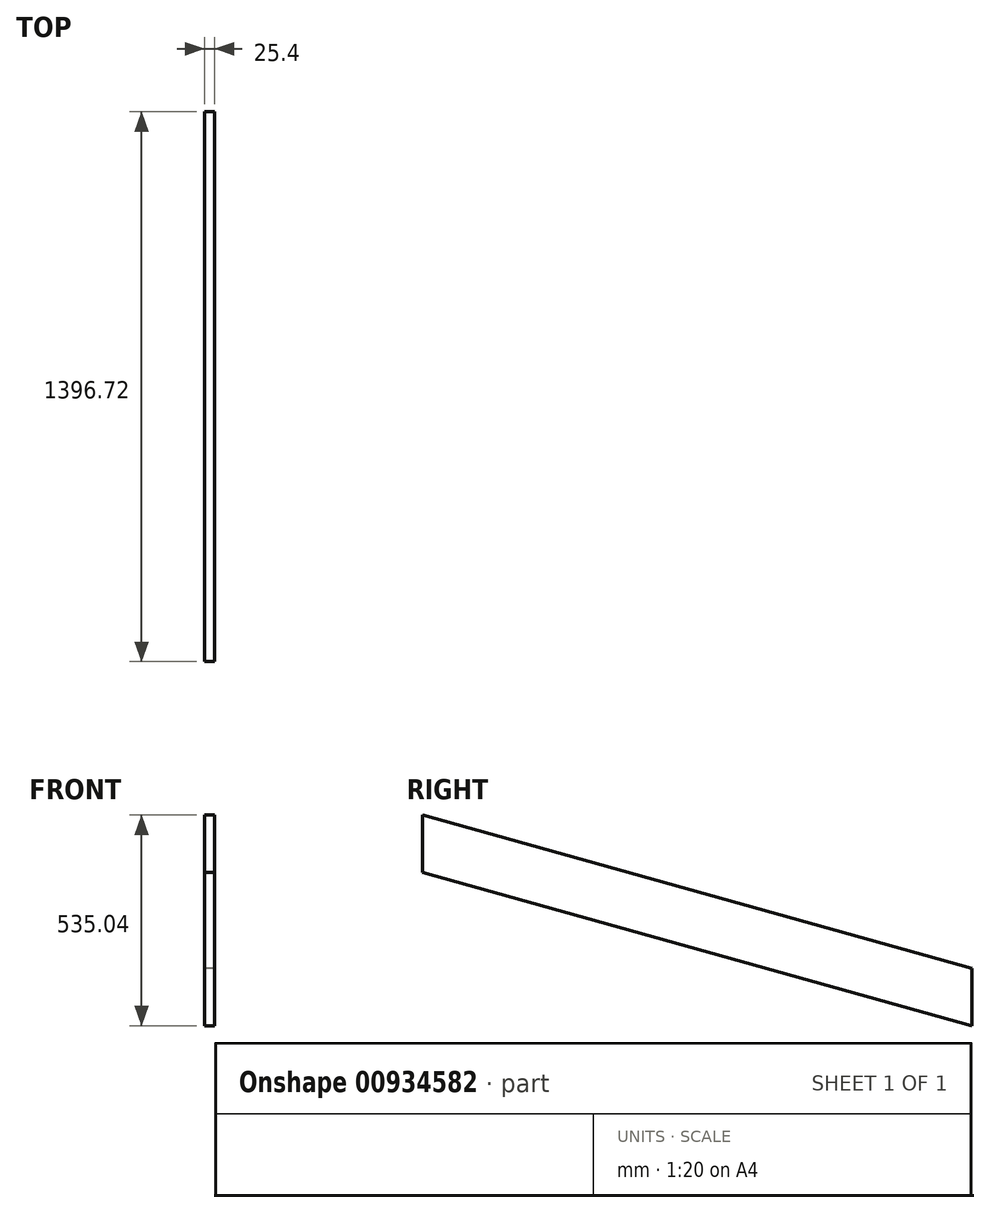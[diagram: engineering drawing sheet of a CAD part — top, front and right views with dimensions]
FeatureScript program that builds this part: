
annotation { "Feature Type Name" : "Feature", "Feature Type Description" : "" }
export const myFeature = defineFeature(function(context is Context, id is Id, definition is map)
    precondition{}
    {
        {
            var Q0;
            Q0=qCreatedBy(makeId("Right.planeOp"),FACE);
            var sketch = newSketch(context, id + "F0", { "sketchPlane" : qUnion([Q0])});
            skLineSegment(sketch, "E0", {"start": v(1396.72, -545.47) * mm, "end": v(0, -155.47) * mm});
            skLineSegment(sketch, "E1.0", {"start": v(1396.72, -400.43) * mm, "end": v(0, -10.43) * mm});
            skLineSegment(sketch, "E2", {"start": v(1396.72, -545.47) * mm, "end": v(1396.72, -400.43) * mm});
            skLineSegment(sketch, "E3", {"start": v(0, -155.47) * mm, "end": v(0, -10.43) * mm});
            skSolve(sketch);
        }
        {
            var Q0;
            Q0=makeQuery(id+"F0.imprint","IMPRINT",FACE,{"disambiguationData":[TD([[makeQuery(id+"F0.imprint","IMPRINT",EDGE,{"derivedFrom":sQuery(id+"F0.wireOp",EDGE,"E0")}),-1.0]])]});
            extrude(context, id + "F1", {"entities" : qUnion([Q0]), "depth" : 25.4 * mm, "offsetDistance" : 25.4 * mm});
        }
    });
